# Revit family: MEFA Trägerklammer TKN - TK
name_source: partatom
category: HLS-Bauteile
revit_build: Autodesk Revit 2017 (Build: 20190507_1515(x64)
units: mm (PartAtom-declared; Revit-internal decimal feet)

## family parameters
Basisbauteil = Fläche
Beim Laden mit Abzugskörper schneiden = Nein
Bemaßung runder Anschluss = Durchmesser verwenden
Gemeinsam genutzt = Ja
Raumberechnungspunkt = Nein
Teiletyp = Normal

## types (8) — shared parameters
Anzugsmoment = 0.00 kip-ft
Fabrikat = VS Guss
Firma = MEFA Befestigungs- und Montagesysteme GmbH
Material = Temperguss
Mengeneinheit = St
Oberflaeche = galvanisch verzinkt
Vorgabe-Ansicht = 1219 mm
min. Klemmdicke = 1 mm
vpe = 50 St
zero-valued in all types: Stärke

## per-type parameters (varying)
| type | Artikelnummer | Befestigung | EAN | Gewicht | Gewicht pro Bauteil | Gewinde | Höhe | Kurztext1 | Kurztext2 | Lochdurchmesser | Typ | VdS-Zulassungsnummer | max Klemmdicke | max. zul. Last |
| Durchgangsloch TKN  8 | 0579458 | mit Durchgangsloch | 4250928414618 | 0.09 kg | 0.09 kg | für M8 | 35 mm | Trägerklammer Guss TKN | Klemmbereich 1 - 18 mm Loch für M8 | 9 mm | MEFA Trägerklammer TKN  8 - M 8 : MEFA Trägerklammer TKN  8 | G4000005 | 0 mm  [stored 0 ft] | 0.27 kip |
| Durchgangsloch TKN 10 | 0579460 | mit Durchgangsloch | 4250928414625 | 0.16 kg | 0.16 kg | für M10 | 42 mm | Trägerklammer Guss TKN | Klemmbereich 1 - 20 mm Loch für M10 | 11 mm | MEFA Trägerklammer TKN 10 - M10 : MEFA Trägerklammer TKN 10 | G4000005 | 0 mm  [stored 0 ft] | 0.56 kip |
| Durchgangsloch TK 12 | 0579462 | mit Durchgangsloch | 4250928414632 | 0.24 kg | 0.24 kg | für M12 | 54 mm | Trägerklammer Guss TKN | Klemmbereich 1 - 26 mm Loch für M12 | 13 mm | MEFA Trägerklammer TK 12 - M12 : MEFA Trägerklammer TK 12 | G4910044 | 0 mm  [stored 0 ft] | 0.79 kip |
| mit Gewinde TKN M 8 | 0579558 | mit Gewinde | 4250928414687 | 0.09 kg | 0.09 kg | M8 | 37 mm | Trägerklammer Guss TKN | Klemmbereich 1 - 18 mm M8 |  | MEFA Trägerklammer TKN  8 - M 8 : MEFA Trägerklammer TKN M 8 | G4000005 | 0 mm  [stored 0 ft] | 0.27 kip |
| mit Gewinde TKN M10 | 0579560 | mit Gewinde | 4250928414694 | 0.16 kg | 0.16 kg | M10 | 42 mm | Trägerklammer Guss TKN | Klemmbereich 1 - 20 mm M10 |  | MEFA Trägerklammer TKN 10 - M10 : MEFA Trägerklammer TKN M10 | G4000005 | 0 mm  [stored 0 ft] | 0.56 kip |
| mit Gewinde TK M12 | 0579562 | mit Gewinde | 4250928414700 | 0.24 kg | 0.24 kg | M12 | 54 mm | Trägerklammer Guss TK | Klemmbereich 1 - 26 mm M12 |  | MEFA Trägerklammer TK 12 - M12 : MEFA Trägerklammer TK M12 | G4910044 | 0 mm  [stored 0 ft] | 0.79 kip |
| mit Gewinde TK M16 | 0579548 | mit Gewinde | 4250928414670 | 0.40 kg | 0.40 kg | M16 | 58 mm | Trägerklammer Guss TK | Klemmbereich 1 - 26 mm M16 |  | MEFA Trägerklammer TK 16 - M16 : MEFA Trägerklammer TK M16 | G4030026 | 0 mm  [stored 0 ft] | 1.24 kip |
| Durchgangsloch TK 16 | 0579448 | mit Durchgangsloch | 4250928414601 | 0.40 kg | 0.40 kg | für M16 | 58 mm | Trägerklammer Guss TK | Klemmbereich 1 - 26 mm Loch für M16 | 17 mm | MEFA Trägerklammer TK 16 - M16 : MEFA Trägerklammer TK 16 | G4030026 | 26 mm  [stored 0.0853018 ft] | 1.24 kip |

note: [stored X ft] marks values corroborated as IEEE doubles in the binary element streams (Revit-internal decimal feet)

## geometry (parser evidence)
native form markers: Sweep x9
no freeform markers — native parametric forms only
